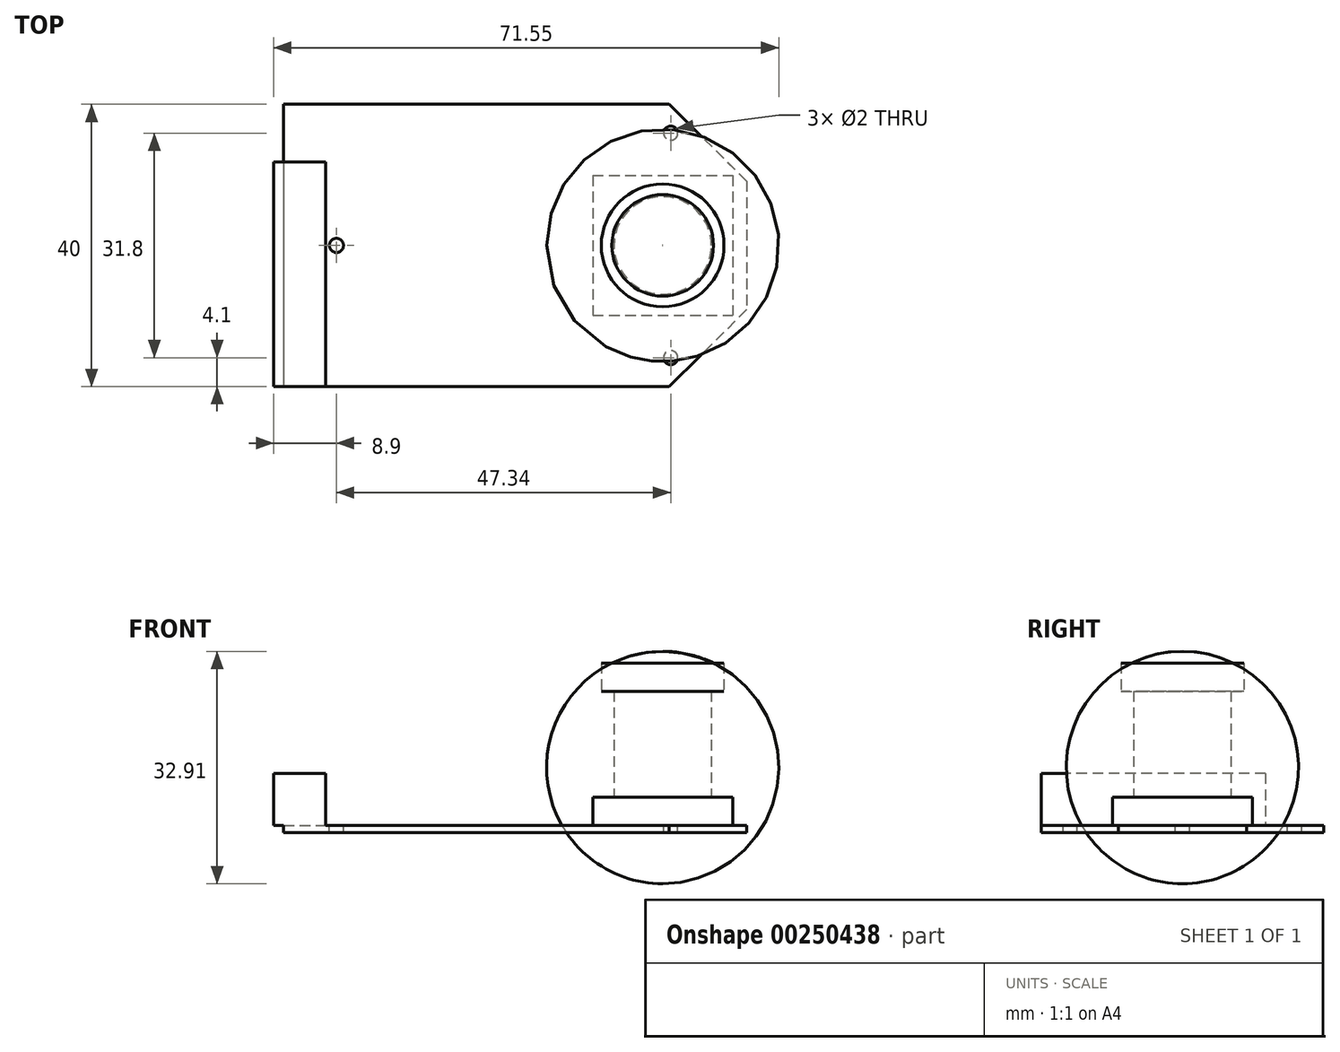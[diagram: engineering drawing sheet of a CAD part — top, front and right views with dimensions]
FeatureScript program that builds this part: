
annotation { "Feature Type Name" : "Feature", "Feature Type Description" : "" }
export const myFeature = defineFeature(function(context is Context, id is Id, definition is map)
    precondition{}
    {
        {
            var Q0;
            Q0=qCreatedBy(makeId("Top.planeOp"),FACE);
            var sketch = newSketch(context, id + "F0", { "sketchPlane" : qUnion([Q0])});
            skLineSegment(sketch, "E0", {"start": v(-32.8, 20) * mm, "end": v(21.8, 20) * mm});
            skLineSegment(sketch, "E1", {"start": v(-32.8, 20) * mm, "end": v(-32.8, -20) * mm});
            skLineSegment(sketch, "E2", {"start": v(-32.8, -20) * mm, "end": v(21.8, -20) * mm});
            skLineSegment(sketch, "E3", {"start": v(32.8, 9.1) * mm, "end": v(32.8, -9.1) * mm});
            skLineSegment(sketch, "E4", {"start": v(32.8, -9.1) * mm, "end": v(21.8, -20) * mm});
            skLineSegment(sketch, "E5", {"start": v(32.8, 9.1) * mm, "end": v(21.8, 20) * mm});
            skSolve(sketch);
        }
        {
            var Q0;
            Q0=makeQuery(id+"F0.imprint","IMPRINT",FACE,{"disambiguationData":[TD([[makeQuery(id+"F0.imprint","IMPRINT",EDGE,{"derivedFrom":sQuery(id+"F0.wireOp",EDGE,"E0")}),-1.0]])]});
            extrude(context, id + "F1", {"entities" : qUnion([Q0]), "depth" : 1 * mm});
        }
        {
            var Q0;
            Q0=makeQuery(id+"F1.opExtrude","CAP_FACE",FACE,{"disambiguationData":[OSD([sQuery(id+"F0.wireOp",EDGE,"E0"),sQuery(id+"F0.wireOp",EDGE,"E1"),sQuery(id+"F0.wireOp",EDGE,"E2"),sQuery(id+"F0.wireOp",EDGE,"E3"),sQuery(id+"F0.wireOp",EDGE,"E4"),sQuery(id+"F0.wireOp",EDGE,"E5")])],"isStart":false});
            var sketch = newSketch(context, id + "F2", { "sketchPlane" : qUnion([Q0])});
            skLineSegment(sketch, "E6.bottom", {"start": v(11, 9.9) * mm, "end": v(30.8, 9.9) * mm});
            skLineSegment(sketch, "E6.top", {"start": v(11, -9.9) * mm, "end": v(30.8, -9.9) * mm});
            skLineSegment(sketch, "E6.left", {"start": v(11, 9.9) * mm, "end": v(11, -9.9) * mm});
            skLineSegment(sketch, "E6.right", {"start": v(30.8, 9.9) * mm, "end": v(30.8, -9.9) * mm});
            skSolve(sketch);
        }
        {
            var Q0;
            Q0=makeQuery(id+"F2.imprint","IMPRINT",FACE,{"disambiguationData":[TD([[makeQuery(id+"F2.imprint","IMPRINT",EDGE,{"derivedFrom":sQuery(id+"F2.wireOp",EDGE,"E6.bottom")}),-1.0]])]});
            extrude(context, id + "F3", {"entities" : qUnion([Q0]), "operationType" : NewBodyOperationType.ADD, "depth" : 4 * mm});
        }
        {
            var Q0;
            Q0=makeQuery(id+"F3.opExtrude","CAP_FACE",FACE,{"disambiguationData":[OSD([sQuery(id+"F2.wireOp",EDGE,"E6.bottom"),sQuery(id+"F2.wireOp",EDGE,"E6.top"),sQuery(id+"F2.wireOp",EDGE,"E6.left"),sQuery(id+"F2.wireOp",EDGE,"E6.right")])],"isStart":false});
            var sketch = newSketch(context, id + "F4", { "sketchPlane" : qUnion([Q0])});
            skCircle(sketch, "E7", {"center": v(20.9, 0) * mm, "radius": 6.9 * mm});
            skPoint(sketch, "E7.centerSnap0", {"position": v(20.9, -9.9) * mm});
            skSolve(sketch);
        }
        {
            var Q0;
            Q0=makeQuery(id+"F4.imprint","IMPRINT",FACE,{"disambiguationData":[TD([[makeQuery(id+"F4.imprint","IMPRINT",EDGE,{"derivedFrom":sQuery(id+"F4.wireOp",EDGE,"E7")}),1.0]])]});
            extrude(context, id + "F5", {"entities" : qUnion([Q0]), "operationType" : NewBodyOperationType.ADD, "depth" : 15 * mm});
        }
        {
            var Q0;
            Q0=makeQuery(id+"F5.opExtrude","CAP_FACE",FACE,{"disambiguationData":[OSD([sQuery(id+"F4.wireOp",EDGE,"E7")])],"isStart":false});
            var sketch = newSketch(context, id + "F6", { "sketchPlane" : qUnion([Q0])});
            skCircle(sketch, "E8", {"center": v(20.9, 0) * mm, "radius": 8.7 * mm});
            skSolve(sketch);
        }
        {
            var Q0;
            Q0=makeQuery(id+"F6.imprint","IMPRINT",FACE,{"disambiguationData":[TD([[makeQuery(id+"F6.imprint","IMPRINT",EDGE,{"derivedFrom":sQuery(id+"F6.wireOp",EDGE,"E8")}),1.0]])]});
            var Q1;
            Q1=makeQuery(id+"F6.imprint","IMPRINT",FACE,{"disambiguationData":[TD([[makeQuery(id+"F6.imprint","IMPRINT",EDGE,{"derivedFrom":makeQuery(id+"F5.opExtrude","CAP_EDGE",EDGE,{"disambiguationData":[OSD([sQuery(id+"F4.wireOp",EDGE,"E7")])],"isStart":false})}),1.0]])]});
            extrude(context, id + "F7", {"entities" : qUnion([Q0, Q1]), "operationType" : NewBodyOperationType.ADD, "depth" : 4 * mm});
        }
        {
            var Q0;
            Q0=makeQuery(id+"F1.opExtrude","CAP_FACE",FACE,{"disambiguationData":[OSD([sQuery(id+"F0.wireOp",EDGE,"E0"),sQuery(id+"F0.wireOp",EDGE,"E1"),sQuery(id+"F0.wireOp",EDGE,"E2"),sQuery(id+"F0.wireOp",EDGE,"E3"),sQuery(id+"F0.wireOp",EDGE,"E4"),sQuery(id+"F0.wireOp",EDGE,"E5")])],"isStart":false});
            var sketch = newSketch(context, id + "F8", { "sketchPlane" : qUnion([Q0])});
            skLineSegment(sketch, "E9.bottom", {"start": v(-34.2, 11.8) * mm, "end": v(-26.85, 11.8) * mm});
            skLineSegment(sketch, "E9.top", {"start": v(-34.2, -20) * mm, "end": v(-26.85, -20) * mm});
            skLineSegment(sketch, "E9.left", {"start": v(-34.2, 11.8) * mm, "end": v(-34.2, -20) * mm});
            skLineSegment(sketch, "E9.right", {"start": v(-26.85, 11.8) * mm, "end": v(-26.85, -20) * mm});
            skSolve(sketch);
        }
        {
            var Q0;
            {var subQ0=sQuery(id+"F8.wireOp",EDGE,"E9.left");Q0=makeQuery(id+"F8.imprint","IMPRINT",FACE,{"disambiguationData":[TD([[makeQuery(id+"F8.imprint","IMPRINT",EDGE,{"derivedFrom":subQ0}),1.0]])]});}
            var Q1;
            {var subQ0=sQuery(id+"F8.wireOp",EDGE,"E9.right");Q1=makeQuery(id+"F8.imprint","IMPRINT",FACE,{"disambiguationData":[TD([[makeQuery(id+"F8.imprint","IMPRINT",EDGE,{"derivedFrom":subQ0}),-1.0]])]});}
            extrude(context, id + "F9", {"entities" : qUnion([Q0, Q1]), "operationType" : NewBodyOperationType.ADD, "depth" : 7.37 * mm});
        }
        {
            var Q0;
            Q0=makeQuery(id+"F1.opExtrude","CAP_FACE",FACE,{"disambiguationData":[OSD([sQuery(id+"F0.wireOp",EDGE,"E0"),sQuery(id+"F0.wireOp",EDGE,"E1"),sQuery(id+"F0.wireOp",EDGE,"E2"),sQuery(id+"F0.wireOp",EDGE,"E3"),sQuery(id+"F0.wireOp",EDGE,"E4"),sQuery(id+"F0.wireOp",EDGE,"E5")])],"isStart":false});
            var sketch = newSketch(context, id + "F10", { "sketchPlane" : qUnion([Q0])});
            skCircle(sketch, "E10", {"center": v(-25.3, 0) * mm, "radius": 1 * mm});
            skPoint(sketch, "E10.centerSnap0", {"position": v(-26.85, -4.1) * mm});
            skCircle(sketch, "E11", {"center": v(22.04, 15.9) * mm, "radius": 1 * mm});
            skCircle(sketch, "E12", {"center": v(22.04, -15.9) * mm, "radius": 1 * mm});
            skSolve(sketch);
        }
        {
            var Q0;
            Q0 = qSketchRegion(id + "F10", true);
            extrude(context, id + "F11", {"entities" : qUnion([Q0]), "operationType" : NewBodyOperationType.REMOVE, "oppositeDirection" : true, "depth" : 25 * mm});
        }
        {
            var Q0;
            Q0=qCreatedBy(makeId("Front.planeOp"),FACE);
            var sketch = newSketch(context, id + "F12", { "sketchPlane" : qUnion([Q0])});
            skLineSegment(sketch, "E13.0", {"start": v(20.9, 24) * mm, "end": v(28.09, 24) * mm});
            skLineSegment(sketch, "E14", {"start": v(20.9, 49.83) * mm, "end": v(20.9, -46.84) * mm, "construction": true});
            skPoint(sketch, "E15.orphan", {"position": v(12.2, 24) * mm});
            skLineSegment(sketch, "E16", {"start": v(20.9, 25.65) * mm, "end": v(20.9, 24) * mm});
            skArc(sketch, "E17", {"start": v(28.09, 24) * mm, "mid": v(24.59, 25.23) * mm, "end": v(20.9, 25.65) * mm});
            skPoint(sketch, "E18.orphan", {"position": v(29.59, 24) * mm});
            skSolve(sketch);
        }
        {
            var Q0;
            Q0=makeQuery(id+"F12.imprint","IMPRINT",FACE,{"disambiguationData":[TD([[makeQuery(id+"F12.imprint","IMPRINT",EDGE,{"derivedFrom":sQuery(id+"F12.wireOp",EDGE,"E13.0")}),1.0]])]});
            var Q1;
            Q1=sQuery(id+"F12.wireOp",EDGE,"E14");
            revolve(context, id + "F13", {"operationType" : NewBodyOperationType.ADD, "entities" : qUnion([Q0]), "axis" : qUnion([Q1]), "revolveType" : RevolveType.FULL});
        }
    });
